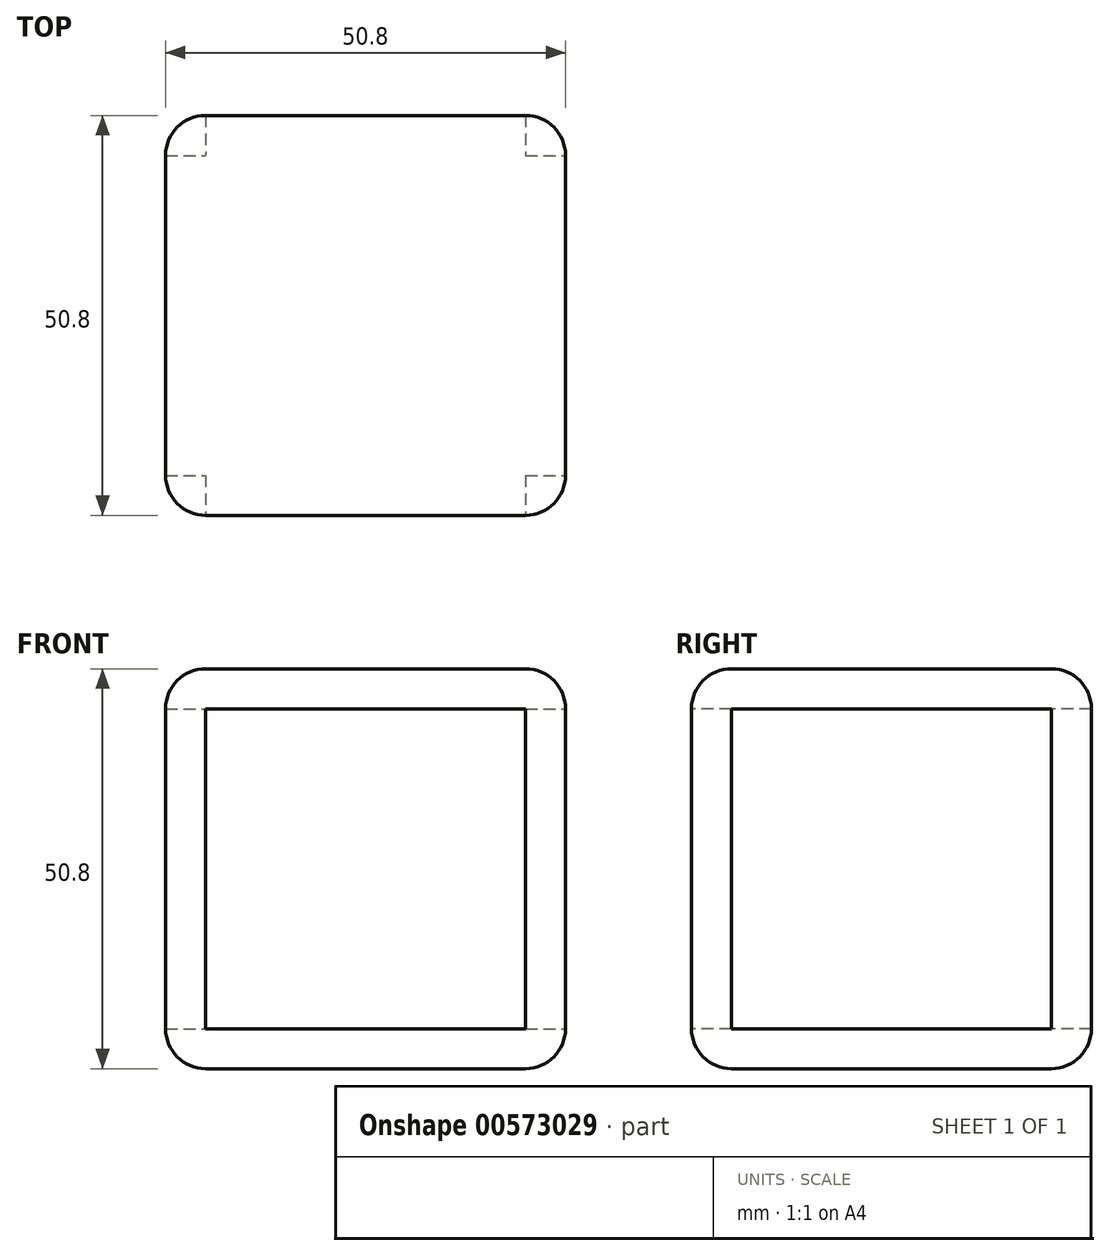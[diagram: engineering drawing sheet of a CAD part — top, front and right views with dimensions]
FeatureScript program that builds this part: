
annotation { "Feature Type Name" : "Feature", "Feature Type Description" : "" }
export const myFeature = defineFeature(function(context is Context, id is Id, definition is map)
    precondition{}
    {
        {
            var Q0;
            Q0=qCreatedBy(makeId("Front.planeOp"),FACE);
            var sketch = newSketch(context, id + "F0", { "sketchPlane" : qUnion([Q0])});
            skLineSegment(sketch, "E0.bottom", {"start": v(0, 0) * mm, "end": v(50.8, 0) * mm});
            skLineSegment(sketch, "E0.top", {"start": v(0, 50.8) * mm, "end": v(50.8, 50.8) * mm});
            skLineSegment(sketch, "E0.left", {"start": v(0, 0) * mm, "end": v(0, 50.8) * mm});
            skLineSegment(sketch, "E0.right", {"start": v(50.8, 0) * mm, "end": v(50.8, 50.8) * mm});
            skSolve(sketch);
        }
        {
            var Q0;
            Q0 = qSketchRegion(id + "F0", true);
            extrude(context, id + "F1", {"entities" : qUnion([Q0]), "depth" : 50.8 * mm, "offsetDistance" : 25.4 * mm});
        }
        {
            var Q0;
            Q0=makeQuery(id+"F1.opExtrude","CAP_FACE",FACE,{"disambiguationData":[OSD([sQuery(id+"F0.wireOp",EDGE,"E0.bottom"),sQuery(id+"F0.wireOp",EDGE,"E0.top"),sQuery(id+"F0.wireOp",EDGE,"E0.left"),sQuery(id+"F0.wireOp",EDGE,"E0.right")])],"isStart":false});
            var sketch = newSketch(context, id + "F2", { "sketchPlane" : qUnion([Q0])});
            skLineSegment(sketch, "E1.bottom", {"start": v(5.08, 45.72) * mm, "end": v(45.72, 45.72) * mm});
            skLineSegment(sketch, "E1.top", {"start": v(5.08, 5.08) * mm, "end": v(45.72, 5.08) * mm});
            skLineSegment(sketch, "E1.left", {"start": v(5.08, 45.72) * mm, "end": v(5.08, 5.08) * mm});
            skLineSegment(sketch, "E1.right", {"start": v(45.72, 45.72) * mm, "end": v(45.72, 5.08) * mm});
            skSolve(sketch);
        }
        {
            var Q0;
            Q0 = qSketchRegion(id + "F2", true);
            extrude(context, id + "F3", {"entities" : qUnion([Q0]), "operationType" : NewBodyOperationType.REMOVE, "oppositeDirection" : true, "depth" : 50.8 * mm, "offsetDistance" : 25.4 * mm});
        }
        {
            var Q0;
            Q0=makeQuery(id+"F1.opExtrude","SWEPT_FACE",FACE,{"disambiguationData":[OSD([sQuery(id+"F0.wireOp",EDGE,"E0.right")])]});
            var sketch = newSketch(context, id + "F4", { "sketchPlane" : qUnion([Q0])});
            skLineSegment(sketch, "E2.bottom", {"start": v(-45.72, 45.72) * mm, "end": v(-5.08, 45.72) * mm});
            skLineSegment(sketch, "E2.top", {"start": v(-45.72, 5.08) * mm, "end": v(-5.08, 5.08) * mm});
            skLineSegment(sketch, "E2.left", {"start": v(-45.72, 45.72) * mm, "end": v(-45.72, 5.08) * mm});
            skLineSegment(sketch, "E2.right", {"start": v(-5.08, 45.72) * mm, "end": v(-5.08, 5.08) * mm});
            skSolve(sketch);
        }
        {
            var Q0;
            Q0 = qSketchRegion(id + "F4", true);
            extrude(context, id + "F5", {"entities" : qUnion([Q0]), "operationType" : NewBodyOperationType.REMOVE, "oppositeDirection" : true, "depth" : 50.8 * mm, "offsetDistance" : 25.4 * mm});
        }
        {
            var Q0;
            Q0=makeQuery(id+"F1.opExtrude","CAP_EDGE",EDGE,{"disambiguationData":[OSD([sQuery(id+"F0.wireOp",EDGE,"E0.top")])],"isStart":false});
            var Q1;
            Q1=makeQuery(id+"F1.opExtrude","SWEPT_EDGE",EDGE,{"disambiguationData":[OSD([sQuery(id+"F0.wireOp",EDGE,"E0.top"),sQuery(id+"F0.wireOp",EDGE,"E0.right")])]});
            var Q2;
            Q2=makeQuery(id+"F1.opExtrude","CAP_EDGE",EDGE,{"disambiguationData":[OSD([sQuery(id+"F0.wireOp",EDGE,"E0.right")])],"isStart":false});
            var Q3;
            Q3=makeQuery(id+"F1.opExtrude","CAP_EDGE",EDGE,{"disambiguationData":[OSD([sQuery(id+"F0.wireOp",EDGE,"E0.bottom")])],"isStart":false});
            var Q4;
            Q4=makeQuery(id+"F1.opExtrude","SWEPT_EDGE",EDGE,{"disambiguationData":[OSD([sQuery(id+"F0.wireOp",EDGE,"E0.bottom"),sQuery(id+"F0.wireOp",EDGE,"E0.right")])]});
            var Q5;
            Q5=makeQuery(id+"F1.opExtrude","CAP_EDGE",EDGE,{"disambiguationData":[OSD([sQuery(id+"F0.wireOp",EDGE,"E0.bottom")])],"isStart":true});
            var Q6;
            Q6=makeQuery(id+"F1.opExtrude","SWEPT_EDGE",EDGE,{"disambiguationData":[OSD([sQuery(id+"F0.wireOp",EDGE,"E0.bottom"),sQuery(id+"F0.wireOp",EDGE,"E0.left")])]});
            var Q7;
            Q7=makeQuery(id+"F1.opExtrude","CAP_EDGE",EDGE,{"disambiguationData":[OSD([sQuery(id+"F0.wireOp",EDGE,"E0.right")])],"isStart":true});
            var Q8;
            Q8=makeQuery(id+"F1.opExtrude","CAP_EDGE",EDGE,{"disambiguationData":[OSD([sQuery(id+"F0.wireOp",EDGE,"E0.top")])],"isStart":true});
            var Q9;
            Q9=makeQuery(id+"F1.opExtrude","CAP_EDGE",EDGE,{"disambiguationData":[OSD([sQuery(id+"F0.wireOp",EDGE,"E0.left")])],"isStart":true});
            fillet(context, id + "F6", {"entities" : qUnion([Q0, Q1, Q2, Q3, Q4, Q5, Q6, Q7, Q8, Q9]), "radius" : 5.08 * mm, "tangentPropagation" : true, "allowEdgeOverflow" : false});
        }
        {
            var Q0;
            Q0=makeQuery(id+"F1.opExtrude","SWEPT_EDGE",EDGE,{"disambiguationData":[OSD([sQuery(id+"F0.wireOp",EDGE,"E0.top"),sQuery(id+"F0.wireOp",EDGE,"E0.left")])]});
            fillet(context, id + "F7", {"entities" : qUnion([Q0]), "radius" : 5.08 * mm, "tangentPropagation" : true, "allowEdgeOverflow" : false});
        }
    });
